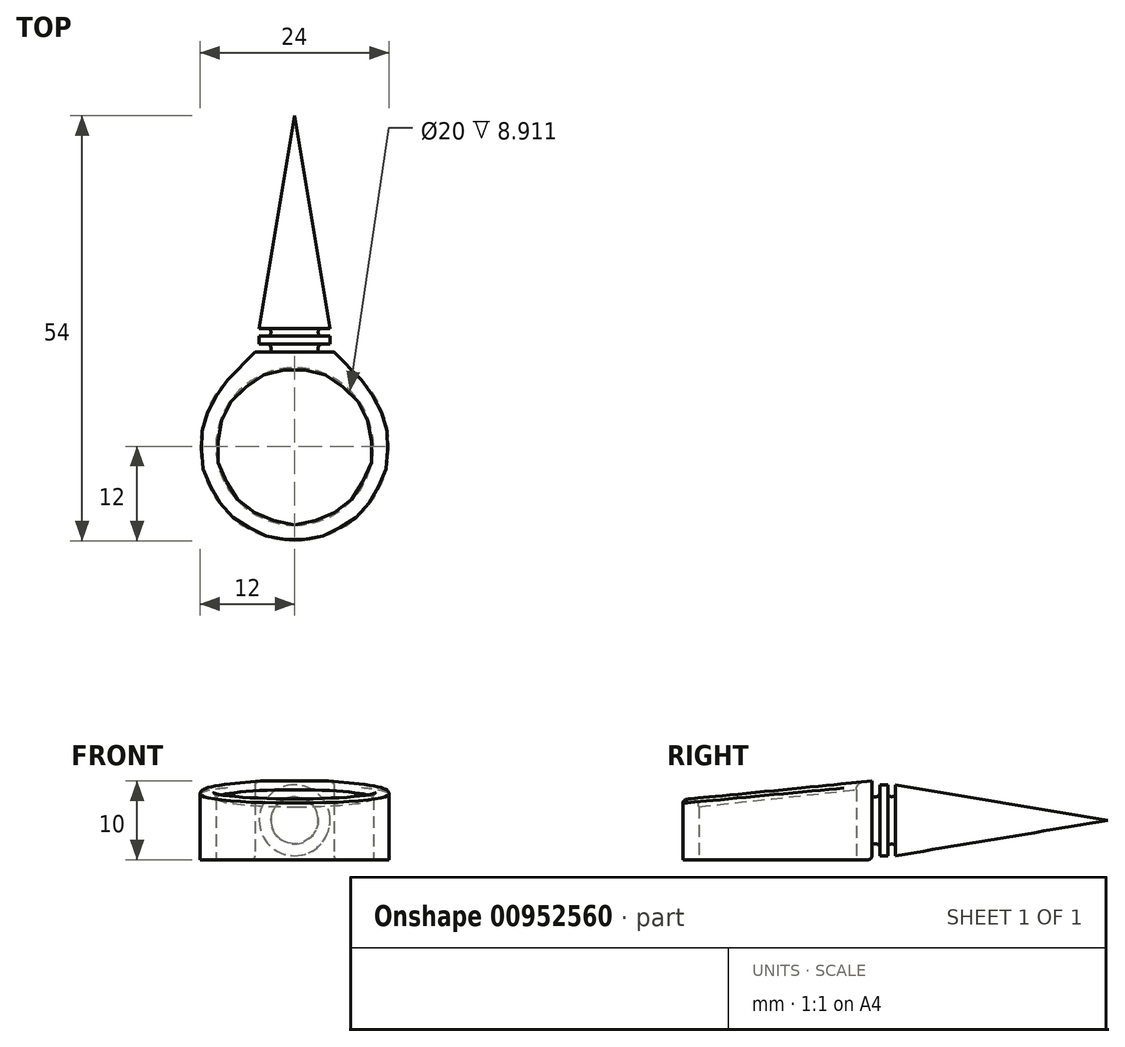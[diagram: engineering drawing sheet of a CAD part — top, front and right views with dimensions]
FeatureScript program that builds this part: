
annotation { "Feature Type Name" : "Feature", "Feature Type Description" : "" }
export const myFeature = defineFeature(function(context is Context, id is Id, definition is map)
    precondition{}
    {
        {
            var Q0;
            Q0=qCreatedBy(makeId("Top.planeOp"),FACE);
            var sketch = newSketch(context, id + "F0", { "sketchPlane" : qUnion([Q0])});
            skCircle(sketch, "E0", {"center": v(0, 0) * mm, "radius": 10 * mm});
            skArc(sketch, "E1", {"start": v(-8.52, 8.45) * mm, "mid": v(0, -12) * mm, "end": v(8.52, 8.45) * mm});
            skLineSegment(sketch, "E2", {"start": v(-5, 12) * mm, "end": v(5, 12) * mm});
            skLineSegment(sketch, "E3", {"start": v(8.52, 8.45) * mm, "end": v(5, 12) * mm});
            skLineSegment(sketch, "E4.trimOffspring", {"start": v(-5, 12) * mm, "end": v(-8.52, 8.45) * mm});
            skSolve(sketch);
        }
        {
            var Q0;
            Q0=makeQuery(id+"F0.imprint","IMPRINT",FACE,{"disambiguationData":[TD([[makeQuery(id+"F0.imprint","IMPRINT",EDGE,{"derivedFrom":sQuery(id+"F0.wireOp",EDGE,"E0")}),-1.0]])]});
            extrude(context, id + "F1", {"entities" : qUnion([Q0]), "endBound" : BoundingType.SYMMETRIC, "depth" : 10 * mm, "offsetDistance" : 25 * mm});
        }
        {
            var Q0;
            Q0=qCreatedBy(makeId("Right.planeOp"),FACE);
            var sketch = newSketch(context, id + "F2", { "sketchPlane" : qUnion([Q0])});
            skLineSegment(sketch, "E5", {"start": v(-13.3, 2.5) * mm, "end": v(21.84, 5.97) * mm});
            skLineSegment(sketch, "E6", {"start": v(-13.3, 2.5) * mm, "end": v(-13.3, 10.5) * mm});
            skLineSegment(sketch, "E7", {"start": v(-13.3, 10.5) * mm, "end": v(21.88, 10.5) * mm});
            skLineSegment(sketch, "E8", {"start": v(21.88, 10.5) * mm, "end": v(21.84, 5.97) * mm});
            skSolve(sketch);
        }
        {
            var Q0;
            Q0 = qSketchRegion(id + "F2", true);
            extrude(context, id + "F3", {"entities" : qUnion([Q0]), "operationType" : NewBodyOperationType.REMOVE, "endBound" : BoundingType.SYMMETRIC, "oppositeDirection" : true, "depth" : 30 * mm, "offsetDistance" : 25 * mm});
        }
        {
            var Q0;
            Q0=makeQuery(id+"F3.boolean.opBoolean","INTERSECT",EDGE,{"derivedFrom":[makeQuery(id+"F1.opExtrude","SWEPT_FACE",FACE,{"disambiguationData":[OSD([sQuery(id+"F0.wireOp",EDGE,"E0")])]}),makeQuery(id+"F3.opExtrude","SWEPT_FACE",FACE,{"disambiguationData":[OSD([sQuery(id+"F2.wireOp",EDGE,"E5")])]})]});
            var Q1;
            Q1=makeQuery(id+"Fv1N4DaBdOC7Az7_1.1.F3.boolean.opBoolean","INTERSECT",EDGE,{"derivedFrom":[makeQuery(id+"F1.opExtrude","SWEPT_FACE",FACE,{"disambiguationData":[OSD([sQuery(id+"F0.wireOp",EDGE,"E0")])]}),makeQuery(id+"Fv1N4DaBdOC7Az7_1.1.F3.opExtrude","SWEPT_FACE",FACE,{"disambiguationData":[OSD([sQuery(id+"F2.wireOp",EDGE,"E5")])]})]});
            fillet(context, id + "F4", {"entities" : qUnion([Q0, Q1]), "radius" : 1 * mm, "tangentPropagation" : true, "allowEdgeOverflow" : false});
        }
        {
            var Q0;
            Q0=qCreatedBy(makeId("Right.planeOp"),FACE);
            var sketch = newSketch(context, id + "F5", { "sketchPlane" : qUnion([Q0])});
            skLineSegment(sketch, "E9", {"start": v(12, 3) * mm, "end": v(13, 3) * mm});
            skLineSegment(sketch, "E10", {"start": v(13, 3) * mm, "end": v(13, 4.5) * mm});
            skLineSegment(sketch, "E11", {"start": v(13, 4.5) * mm, "end": v(14, 4.5) * mm});
            skLineSegment(sketch, "E12", {"start": v(14, 4.5) * mm, "end": v(14, 3) * mm});
            skLineSegment(sketch, "E13", {"start": v(14, 3) * mm, "end": v(15, 3) * mm});
            skLineSegment(sketch, "E14", {"start": v(15, 3) * mm, "end": v(15, 4.5) * mm});
            skLineSegment(sketch, "E15", {"start": v(15, 4.5) * mm, "end": v(42, 0) * mm});
            skLineSegment(sketch, "E16", {"start": v(42, 0) * mm, "end": v(12, 0) * mm});
            skLineSegment(sketch, "E17", {"start": v(12, 0) * mm, "end": v(12, 3) * mm});
            skSolve(sketch);
        }
        {
            var Q0;
            Q0=makeQuery(id+"F5.imprint","IMPRINT",FACE,{"disambiguationData":[TD([[makeQuery(id+"F5.imprint","IMPRINT",EDGE,{"derivedFrom":sQuery(id+"F5.wireOp",EDGE,"E9")}),-1.0]])]});
            var Q1;
            Q1=sQuery(id+"F5.wireOp",EDGE,"E16");
            revolve(context, id + "F6", {"operationType" : NewBodyOperationType.ADD, "surfaceOperationType" : NewSurfaceOperationType.NEW, "entities" : qUnion([Q0]), "axis" : qUnion([Q1]), "revolveType" : RevolveType.FULL});
        }
        {
            var Q0;
            Q0=makeQuery(id+"F6.opRevolve","SWEPT_EDGE",EDGE,{"disambiguationData":[OSD([sQuery(id+"F5.wireOp",EDGE,"E9"),sQuery(id+"F5.wireOp",EDGE,"E17")])]});
            var Q1;
            Q1=makeQuery(id+"F6.opRevolve","SWEPT_EDGE",EDGE,{"disambiguationData":[OSD([sQuery(id+"F5.wireOp",EDGE,"E9"),sQuery(id+"F5.wireOp",EDGE,"E10")])]});
            var Q2;
            Q2=makeQuery(id+"F6.opRevolve","SWEPT_EDGE",EDGE,{"disambiguationData":[OSD([sQuery(id+"F5.wireOp",EDGE,"E12"),sQuery(id+"F5.wireOp",EDGE,"E13")])]});
            var Q3;
            Q3=makeQuery(id+"F6.opRevolve","SWEPT_EDGE",EDGE,{"disambiguationData":[OSD([sQuery(id+"F5.wireOp",EDGE,"E13"),sQuery(id+"F5.wireOp",EDGE,"E14")])]});
            fillet(context, id + "F7", {"entities" : qUnion([Q0, Q1, Q2, Q3]), "radius" : 0.5 * mm, "tangentPropagation" : true, "allowEdgeOverflow" : false});
        }
        {
            var Q0;
            Q0=makeQuery(id+"F1.opExtrude","CAP_EDGE",EDGE,{"disambiguationData":[OSD([sQuery(id+"F0.wireOp",EDGE,"E2")])],"isStart":false});
            var Q1;
            Q1=makeQuery(id+"F3.boolean.opBoolean","INTERSECT",EDGE,{"derivedFrom":[makeQuery(id+"F1.opExtrude","SWEPT_FACE",FACE,{"disambiguationData":[OSD([sQuery(id+"F0.wireOp",EDGE,"E3")])]}),makeQuery(id+"F3.opExtrude","SWEPT_FACE",FACE,{"disambiguationData":[OSD([sQuery(id+"F2.wireOp",EDGE,"E5")])]})]});
            var Q2;
            Q2=makeQuery(id+"F3.boolean.opBoolean","INTERSECT",EDGE,{"derivedFrom":[makeQuery(id+"F1.opExtrude","SWEPT_FACE",FACE,{"disambiguationData":[OSD([sQuery(id+"F0.wireOp",EDGE,"E1")])]}),makeQuery(id+"F3.opExtrude","SWEPT_FACE",FACE,{"disambiguationData":[OSD([sQuery(id+"F2.wireOp",EDGE,"E5")])]})]});
            var Q3;
            Q3=makeQuery(id+"F3.boolean.opBoolean","INTERSECT",EDGE,{"derivedFrom":[makeQuery(id+"F1.opExtrude","SWEPT_FACE",FACE,{"disambiguationData":[OSD([sQuery(id+"F0.wireOp",EDGE,"E4.trimOffspring")])]}),makeQuery(id+"F3.opExtrude","SWEPT_FACE",FACE,{"disambiguationData":[OSD([sQuery(id+"F2.wireOp",EDGE,"E5")])]})]});
            var Q4;
            Q4=makeQuery(id+"Fv1N4DaBdOC7Az7_1.1.F3.boolean.opBoolean","INTERSECT",EDGE,{"derivedFrom":[makeQuery(id+"F1.opExtrude","SWEPT_FACE",FACE,{"disambiguationData":[OSD([sQuery(id+"F0.wireOp",EDGE,"E1")])]}),makeQuery(id+"Fv1N4DaBdOC7Az7_1.1.F3.opExtrude","SWEPT_FACE",FACE,{"disambiguationData":[OSD([sQuery(id+"F2.wireOp",EDGE,"E5")])]})]});
            var Q5;
            Q5=makeQuery(id+"Fv1N4DaBdOC7Az7_1.1.F3.boolean.opBoolean","INTERSECT",EDGE,{"derivedFrom":[makeQuery(id+"F1.opExtrude","SWEPT_FACE",FACE,{"disambiguationData":[OSD([sQuery(id+"F0.wireOp",EDGE,"E3")])]}),makeQuery(id+"Fv1N4DaBdOC7Az7_1.1.F3.opExtrude","SWEPT_FACE",FACE,{"disambiguationData":[OSD([sQuery(id+"F2.wireOp",EDGE,"E5")])]})]});
            var Q6;
            Q6=makeQuery(id+"F1.opExtrude","CAP_EDGE",EDGE,{"disambiguationData":[OSD([sQuery(id+"F0.wireOp",EDGE,"E2")])],"isStart":true});
            var Q7;
            Q7=makeQuery(id+"Fv1N4DaBdOC7Az7_1.1.F3.boolean.opBoolean","INTERSECT",EDGE,{"derivedFrom":[makeQuery(id+"F1.opExtrude","SWEPT_FACE",FACE,{"disambiguationData":[OSD([sQuery(id+"F0.wireOp",EDGE,"E4.trimOffspring")])]}),makeQuery(id+"Fv1N4DaBdOC7Az7_1.1.F3.opExtrude","SWEPT_FACE",FACE,{"disambiguationData":[OSD([sQuery(id+"F2.wireOp",EDGE,"E5")])]})]});
            fillet(context, id + "F8", {"entities" : qUnion([Q0, Q1, Q2, Q3, Q4, Q5, Q6, Q7]), "radius" : 0.5 * mm, "tangentPropagation" : true, "allowEdgeOverflow" : false});
        }
    });
